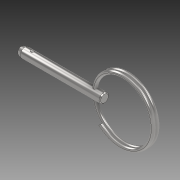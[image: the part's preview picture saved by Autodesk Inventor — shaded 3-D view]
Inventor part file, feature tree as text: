
AUTODESK INVENTOR PART (.ipt)
format: ipt  version: 2020 (Build 240168000, 168)  size: 252,928 bytes
history: mixed  units: in
note: dims shown in document units (in); Inventor stores cm internally (conversion verified against a paired STEP export)
features: revolve x1, other x1, sweep x1, imported_body x1
ambient origin geometry x8: Origin, YZ Plane, XZ Plane, XY Plane, X Axis, Y Axis, Z Axis, Center Point
bodies: Solid1 (imported_parasolid), Solid2 (imported_parasolid), Solid3 (imported_parasolid)
feature tree (4):
  revolve  "Revolve2"  [1 undecoded]
  other  "Cut-Revolve2"
  sweep  "Sweep2"
  imported_body  NMx_Import_Brep_tag  [imported B-rep: ~7 faces, bbox_mm=None]
note: 1 required parameter value undecoded (feature->parameter linkage not recoverable at this tier; creation-order binding heuristic only, values carry confidence <= 0.55)
